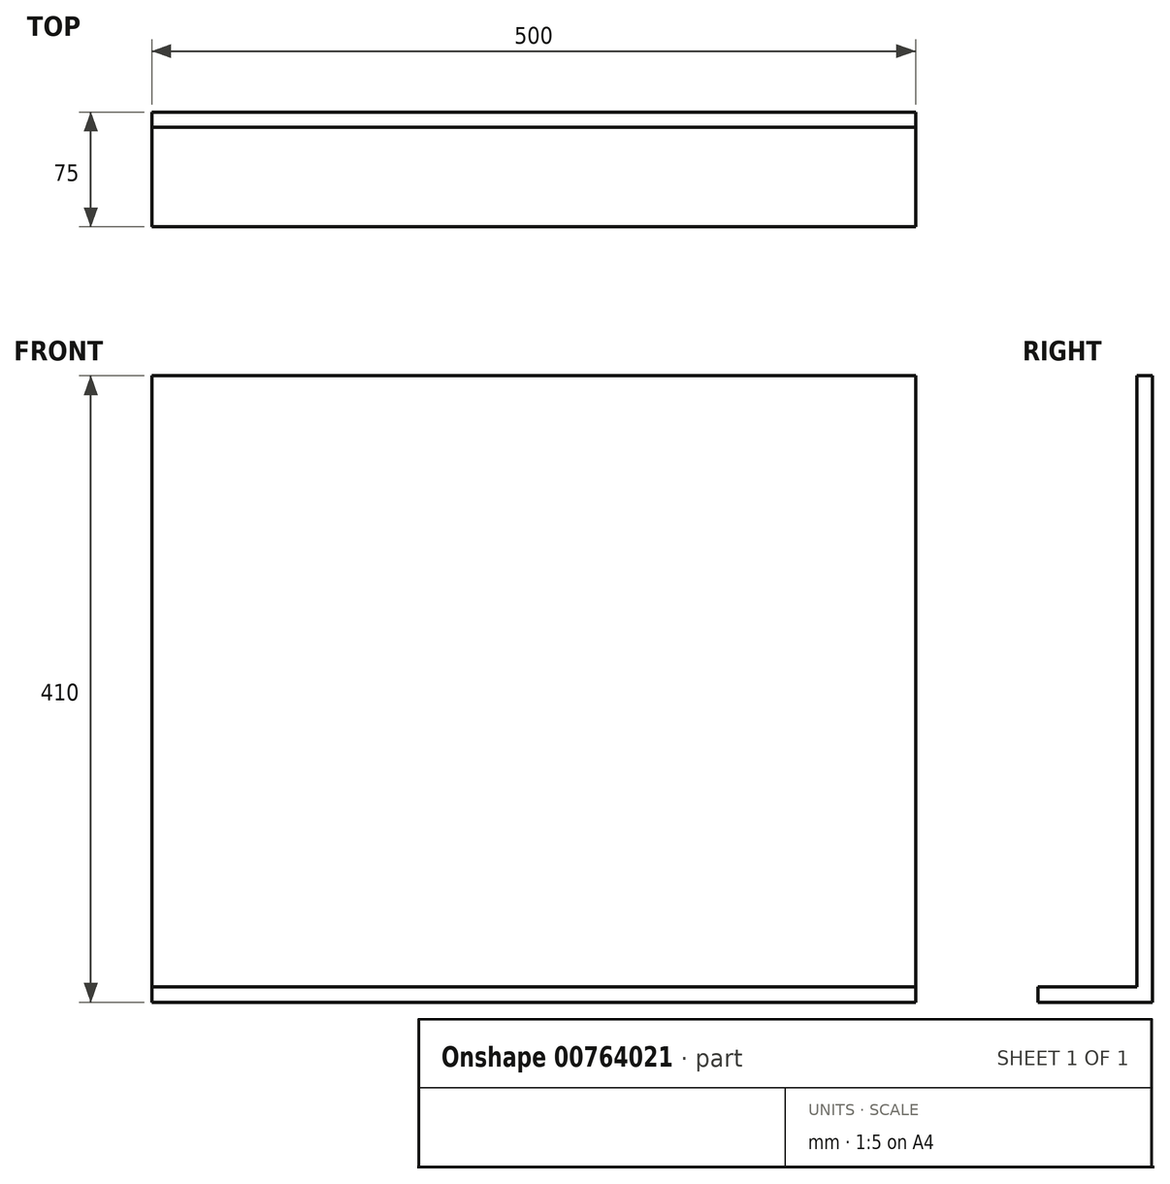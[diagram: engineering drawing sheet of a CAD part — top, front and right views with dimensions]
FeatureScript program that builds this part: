
annotation { "Feature Type Name" : "Feature", "Feature Type Description" : "" }
export const myFeature = defineFeature(function(context is Context, id is Id, definition is map)
    precondition{}
    {
        {
            var Q0;
            Q0=qCreatedBy(makeId("Right.planeOp"),FACE);
            var sketch = newSketch(context, id + "F0", { "sketchPlane" : qUnion([Q0])});
            skLineSegment(sketch, "E0", {"start": v(0, 0) * mm, "end": v(-65, 0) * mm});
            skLineSegment(sketch, "E1", {"start": v(-65, 0) * mm, "end": v(-65, -10) * mm});
            skLineSegment(sketch, "E2", {"start": v(-65, -10) * mm, "end": v(10, -10) * mm});
            skLineSegment(sketch, "E3", {"start": v(10, -10) * mm, "end": v(10, 400) * mm});
            skLineSegment(sketch, "E4", {"start": v(10, 400) * mm, "end": v(0, 400) * mm});
            skLineSegment(sketch, "E5", {"start": v(0, 400) * mm, "end": v(0, 0) * mm});
            skSolve(sketch);
        }
        {
            var Q0;
            Q0=qSketchRegion(id+"F0",true);
            extrude(context, id + "F1", {"entities" : qUnion([Q0]), "endBound" : BoundingType.SYMMETRIC, "depth" : 500 * mm, "offsetDistance" : 25 * mm});
        }
        {
            var Q0;
            Q0=makeQuery(id+"F1.opExtrude","SWEPT_FACE",FACE,{"disambiguationData":[OSD([sQuery(id+"F0.wireOp",EDGE,"E5")])]});
            var sketch = newSketch(context, id + "F2", { "sketchPlane" : qUnion([Q0])});
            skLineSegment(sketch, "E6", {"start": v(0, 0) * mm, "end": v(0, 400) * mm, "construction": true});
            skPoint(sketch, "E7", {"position": v(0, 35) * mm});
            skPoint(sketch, "E8", {"position": v(0, 335) * mm});
            skSolve(sketch);
        }
    });
